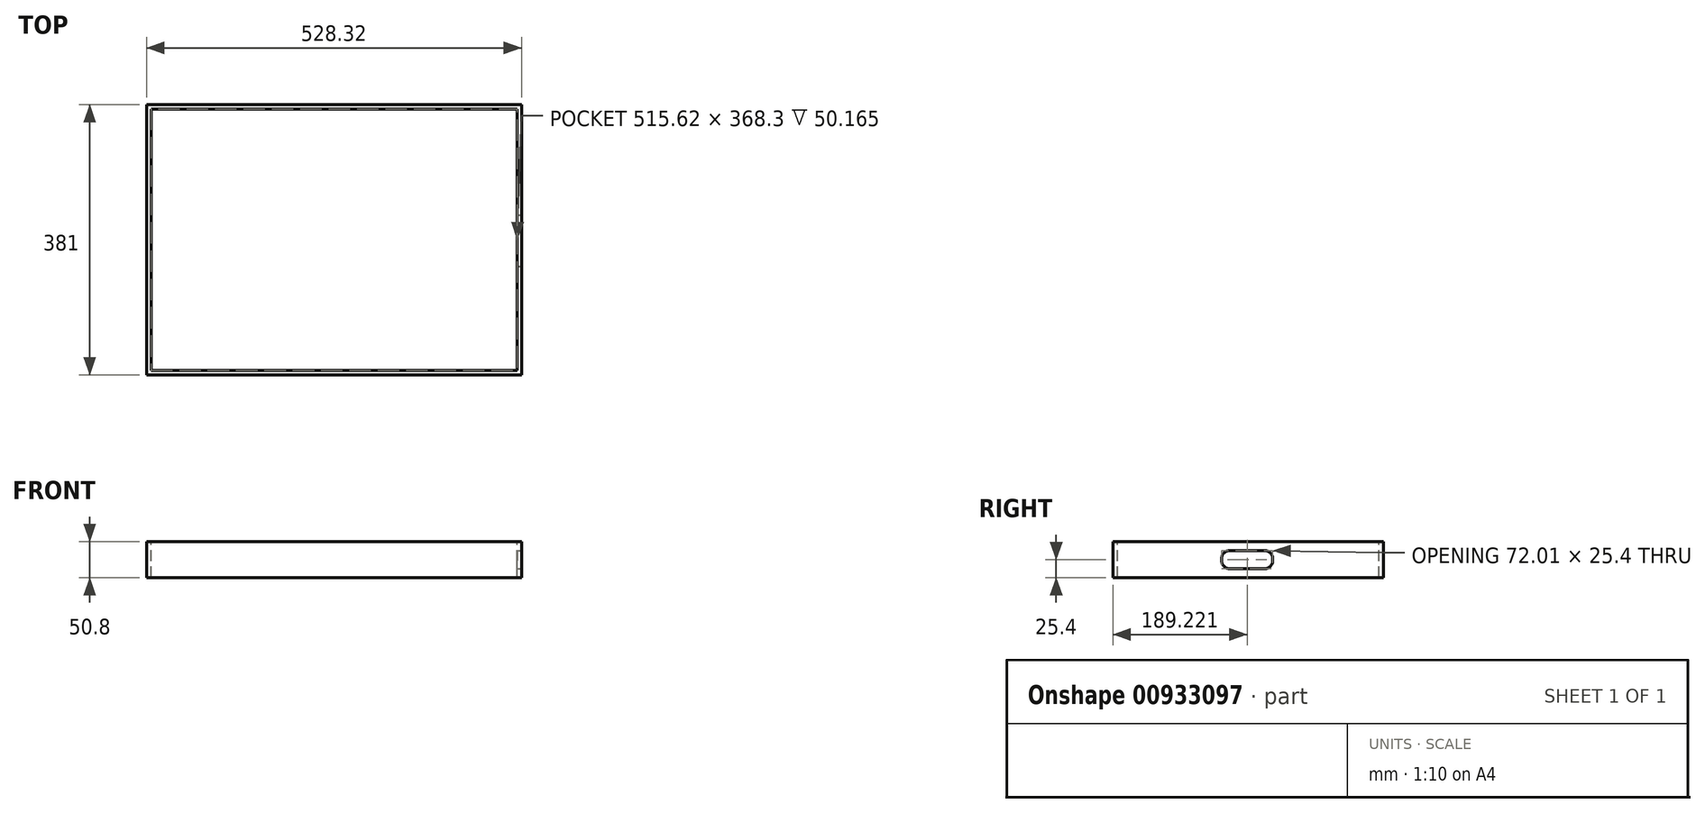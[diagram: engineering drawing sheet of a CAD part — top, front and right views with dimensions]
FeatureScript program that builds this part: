
annotation { "Feature Type Name" : "Feature", "Feature Type Description" : "" }
export const myFeature = defineFeature(function(context is Context, id is Id, definition is map)
    precondition{}
    {
        {
            var Q0;
            Q0=qCreatedBy(makeId("Top.planeOp"),FACE);
            var sketch = newSketch(context, id + "F0", { "sketchPlane" : qUnion([Q0])});
            skLineSegment(sketch, "E0.bottom", {"start": v(-264.16, 190.5) * mm, "end": v(264.16, 190.5) * mm});
            skLineSegment(sketch, "E0.top", {"start": v(-264.16, -190.5) * mm, "end": v(264.16, -190.5) * mm});
            skLineSegment(sketch, "E0.left", {"start": v(-264.16, 190.5) * mm, "end": v(-264.16, -190.5) * mm});
            skLineSegment(sketch, "E0.right", {"start": v(264.16, 190.5) * mm, "end": v(264.16, -190.5) * mm});
            skSolve(sketch);
        }
        {
            var Q0;
            Q0=makeQuery(id+"F0.imprint","IMPRINT",FACE,{"disambiguationData":[TD([[makeQuery(id+"F0.imprint","IMPRINT",EDGE,{"derivedFrom":sQuery(id+"F0.wireOp",EDGE,"E0.bottom")}),-1.0]])]});
            extrude(context, id + "F1", {"entities" : qUnion([Q0]), "depth" : 50.8 * mm, "offsetDistance" : 25.4 * mm});
        }
        {
            var Q0;
            Q0=makeQuery(id+"F1.opExtrude","CAP_FACE",FACE,{"disambiguationData":[OSD([sQuery(id+"F0.wireOp",EDGE,"E0.bottom"),sQuery(id+"F0.wireOp",EDGE,"E0.top"),sQuery(id+"F0.wireOp",EDGE,"E0.left"),sQuery(id+"F0.wireOp",EDGE,"E0.right")])],"isStart":false});
            var sketch = newSketch(context, id + "F2", { "sketchPlane" : qUnion([Q0])});
            skLineSegment(sketch, "E1.0", {"start": v(-257.81, 184.15) * mm, "end": v(257.81, 184.15) * mm});
            skLineSegment(sketch, "E1.1", {"start": v(-257.81, 184.15) * mm, "end": v(-257.81, -184.15) * mm});
            skLineSegment(sketch, "E1.2", {"start": v(-257.81, -184.15) * mm, "end": v(257.81, -184.15) * mm});
            skLineSegment(sketch, "E1.3", {"start": v(257.81, 184.15) * mm, "end": v(257.81, -184.15) * mm});
            skSolve(sketch);
        }
        {
            var Q0;
            Q0=makeQuery(id+"F2.imprint","IMPRINT",FACE,{"disambiguationData":[TD([[makeQuery(id+"F2.imprint","IMPRINT",EDGE,{"derivedFrom":sQuery(id+"F2.wireOp",EDGE,"E1.0")}),-1.0]])]});
            extrude(context, id + "F3", {"entities" : qUnion([Q0]), "operationType" : NewBodyOperationType.REMOVE, "oppositeDirection" : true, "depth" : 50.16 * mm, "offsetDistance" : 25.4 * mm});
        }
        {
            var Q0;
            Q0=makeQuery(id+"F1.opExtrude","SWEPT_FACE",FACE,{"disambiguationData":[OSD([sQuery(id+"F0.wireOp",EDGE,"E0.right")])]});
            var sketch = newSketch(context, id + "F4", { "sketchPlane" : qUnion([Q0])});
            skLineSegment(sketch, "E2.bottom", {"start": v(-37.28, 38.1) * mm, "end": v(34.72, 38.1) * mm});
            skLineSegment(sketch, "E2.top", {"start": v(-37.28, 12.7) * mm, "end": v(34.72, 12.7) * mm});
            skLineSegment(sketch, "E2.left", {"start": v(-37.28, 38.1) * mm, "end": v(-37.28, 12.7) * mm});
            skLineSegment(sketch, "E2.right", {"start": v(34.72, 38.1) * mm, "end": v(34.72, 12.7) * mm});
            skSolve(sketch);
        }
        {
            var Q0;
            Q0 = qSketchRegion(id + "F4", true);
            extrude(context, id + "F5", {"entities" : qUnion([Q0]), "operationType" : NewBodyOperationType.REMOVE, "oppositeDirection" : true, "depth" : 6.35 * mm, "offsetDistance" : 25.4 * mm});
        }
        {
            var Q0;
            Q0=makeQuery(id+"F5.boolean.opBoolean","COPY",EDGE,{"derivedFrom":makeQuery(id+"F5.opExtrude","SWEPT_EDGE",EDGE,{"disambiguationData":[OSD([sQuery(id+"F4.wireOp",EDGE,"E2.top"),sQuery(id+"F4.wireOp",EDGE,"E2.right")])]})});
            var Q1;
            Q1=makeQuery(id+"F5.boolean.opBoolean","COPY",EDGE,{"derivedFrom":makeQuery(id+"F5.opExtrude","SWEPT_EDGE",EDGE,{"disambiguationData":[OSD([sQuery(id+"F4.wireOp",EDGE,"E2.top"),sQuery(id+"F4.wireOp",EDGE,"E2.left")])]})});
            var Q2;
            Q2=makeQuery(id+"F5.boolean.opBoolean","COPY",EDGE,{"derivedFrom":makeQuery(id+"F5.opExtrude","SWEPT_EDGE",EDGE,{"disambiguationData":[OSD([sQuery(id+"F4.wireOp",EDGE,"E2.bottom"),sQuery(id+"F4.wireOp",EDGE,"E2.left")])]})});
            var Q3;
            Q3=makeQuery(id+"F5.boolean.opBoolean","COPY",EDGE,{"derivedFrom":makeQuery(id+"F5.opExtrude","SWEPT_EDGE",EDGE,{"disambiguationData":[OSD([sQuery(id+"F4.wireOp",EDGE,"E2.bottom"),sQuery(id+"F4.wireOp",EDGE,"E2.right")])]})});
            fillet(context, id + "F6", {"entities" : qUnion([Q0, Q1, Q2, Q3]), "radius" : 11.43 * mm, "tangentPropagation" : true, "allowEdgeOverflow" : false});
        }
    });
